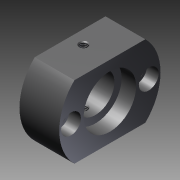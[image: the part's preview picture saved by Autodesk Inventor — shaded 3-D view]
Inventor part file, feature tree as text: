
AUTODESK INVENTOR PART (.ipt)
format: ipt  version: 2016 (Build 200138000, 138)  size: 172,032 bytes
history: native  units: mm
features: other x21, sketch x5, revolve x4, thread x3, extrude x1, pattern_linear x1
ambient origin geometry x8: Origin, YZ Plane, XZ Plane, XY Plane, X Axis, Y Axis, Z Axis, Center Point
bodies: Solid1 (feature_tree)
feature tree (35):
  revolve  "Revolution1"  [1 undecoded]
  extrude  "Extrusion1"  Depth=14.147mm TaperAngle=0.0deg
  revolve  "Revolution2"  Angle=360.0deg
  thread  "Thread1"  [1 undecoded]
  pattern_linear  "Rectangular Pattern1"  Spacing1=0.0mm  [1 undecoded]
  revolve  "Revolution3"  [1 undecoded]
  thread  "Thread2"  [1 undecoded]
  revolve  "Revolution4"  [1 undecoded]
  thread  "Thread3"  [1 undecoded]
  other  "to_bearings_XY"
  other  "to_bearings_YZ"
  other  "to_bearings_ZX"
  other  "to_bearings_X"
  other  "to_bearings_Y"
  other  "to_bearings_Z"
  other  "to_bearings_Center"
  other  "to_screw1_XY"
  other  "to_screw1_YZ"
  other  "to_screw1_ZX"
  other  "to_screw1_X"
  other  "to_screw1_Y"
  other  "to_screw1_Z"
  other  "to_screw1_Center"
  other  "to_screw2_XY"
  other  "to_screw2_YZ"
  other  "to_screw2_ZX"
  other  "to_screw2_X"
  other  "to_screw2_Y"
  other  "to_screw2_Z"
  other  "to_screw2_Center"
  sketch  "Sketch_1"  dims[d0=360.0deg d1=24.0mm d2=0.0mm]
  sketch  "Sketch_2"  dims[d3=360.0deg d4=14.147mm d5=0.0mm]
  sketch  "Sketch_3"  dims[d6=20.0mm d8=43.0mm d9=10.0mm d11=0.0mm d12=360.0deg d13=8.984mm d14=0.0mm]
  sketch  "Sketch_4"  dims[d15=360.0deg]
  sketch  "Sketch_6"  dims[d16=8.984mm d17=0.0mm d18=0.0mm]
note: 7 required parameter values undecoded (feature->parameter linkage not recoverable at this tier; creation-order binding heuristic only, values carry confidence <= 0.55)